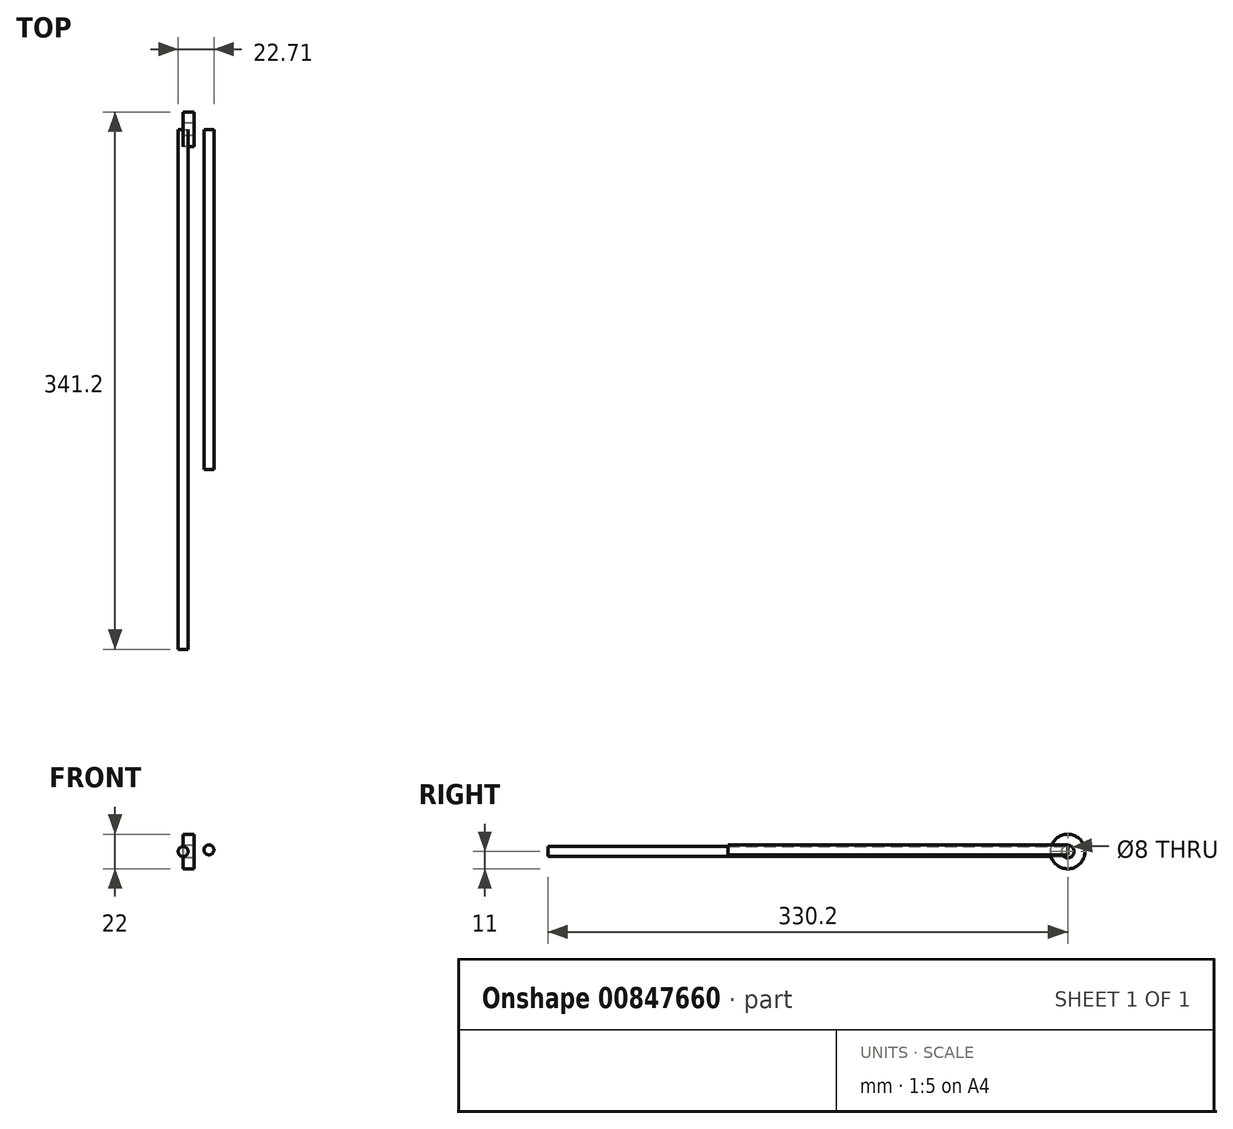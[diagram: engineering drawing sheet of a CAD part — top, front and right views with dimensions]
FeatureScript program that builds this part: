
annotation { "Feature Type Name" : "Feature", "Feature Type Description" : "" }
export const myFeature = defineFeature(function(context is Context, id is Id, definition is map)
    precondition{}
    {
        {
            var Q0;
            Q0=qCreatedBy(makeId("Front.planeOp"),FACE);
            var sketch = newSketch(context, id + "F0", { "sketchPlane" : qUnion([Q0])});
            skCircle(sketch, "E0", {"center": v(0, 0) * mm, "radius": 3.18 * mm});
            skSolve(sketch);
        }
        {
            var Q0;
            Q0 = qSketchRegion(id + "F0", true);
            extrude(context, id + "F1", {"entities" : qUnion([Q0]), "depth" : 330.2 * mm, "offsetDistance" : 25.4 * mm});
        }
        {
            var Q0;
            Q0=qCreatedBy(makeId("Right.planeOp"),FACE);
            var sketch = newSketch(context, id + "F2", { "sketchPlane" : qUnion([Q0])});
            skCircle(sketch, "E1", {"center": v(0, 0) * mm, "radius": 11 * mm});
            skCircle(sketch, "E2", {"center": v(0, 0) * mm, "radius": 4 * mm});
            skSolve(sketch);
        }
        {
            var Q0;
            Q0=makeQuery(id+"F2.imprint","IMPRINT",FACE,{"disambiguationData":[TD([[makeQuery(id+"F2.imprint","IMPRINT",EDGE,{"derivedFrom":sQuery(id+"F2.wireOp",EDGE,"E1")}),1.0]])]});
            var Q1;
            Q1=sQuery(id+"F2.wireOp",EDGE,"E1");
            extrude(context, id + "F3", {"entities" : qUnion([Q0]), "surfaceEntities" : qUnion([Q1]), "depth" : 7 * mm, "offsetDistance" : 25.4 * mm});
        }
        {
            var Q0;
            Q0=qCreatedBy(makeId("Front.planeOp"),FACE);
            var sketch = newSketch(context, id + "F4", { "sketchPlane" : qUnion([Q0])});
            skCircle(sketch, "E3", {"center": v(16.36, 1.1) * mm, "radius": 3.18 * mm});
            skSolve(sketch);
        }
        {
            var Q0;
            Q0 = qSketchRegion(id + "F4", true);
            var Q1;
            Q1=sQuery(id+"F4.wireOp",EDGE,"E3");
            extrude(context, id + "F5", {"entities" : qUnion([Q0]), "surfaceEntities" : qUnion([Q1]), "depth" : 215.9 * mm, "offsetDistance" : 25.4 * mm});
        }
    });
